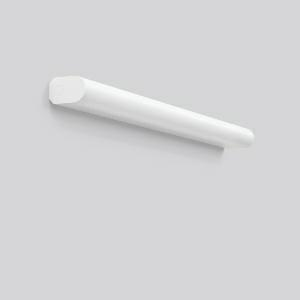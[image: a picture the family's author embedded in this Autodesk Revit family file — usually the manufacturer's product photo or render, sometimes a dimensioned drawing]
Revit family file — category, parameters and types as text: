
# Revit family: rt_44_451169_002_1e48
name_source: partatom
category: Lighting Fixtures
units: mm (PartAtom-declared; Revit-internal decimal feet)

## family parameters
Cut with Voids When Loaded = No
Host = Face
Light Source = No
Part Type = Normal
Room Calculation Point = No
Round Connector Dimension = Use Diameter
Shared = No

## types (1)
- RT 44 (1 x LED Modul 830, 1400 lm, 3000)
    Apparent Load = 15 VA
    CIE Flux Codes = 36 65 85 82 100
    Color Rendering = 80
    Color Temperature = 3000
    Default Elevation = 1800 mm
    Description = Series: RT 44
Linear luminaire, can be used as wall and mirror luminaire. Base: aluminium, powder-coated. End caps: plastic (polycarbonate), shock-resistant. Diffuser: plastic (polycarbonate), opal. Suitable for Ceiling mounting, Wall (surface). Can be installed horizontally and vertically. Very easy installation thanks to Plug+Play connection. Driver integrated. High type of protection: IP44 for use in wet areas. 
Colour: pure white (RAL 9010)
Length: 900 mm
Width: 55 mm
Height: 87 mm
Lamp: LED
Socket: without socket
Colour temperature: 3000K
Colour rendering index (CRI): 80
System power: 15 W
Rated luminous flux: 1400 lm
Luminous efficiency: 93 lm/W
Control gear: Regulated power supply
Protection class: I
Type of protection: IP 44
    Height = 87 mm
    Lamp = 1 x LED Modul 830
    Lamp Light Flux = 1400 lm
    Lamp count = 1
    Length = 900 mm
    Lifetime = 50000 h
    Luminous efficacy = 93 lm/W
    Manufacturer = RZB
    ModVariant = No
    Model = 451169.002
    Mounting Place = Ceiling, Wall
    Mounting Type = Surface mounted
    Number of Poles = 1
    OnlyDefault = Yes
    Power Factor = 1
    Product Name = RT 44
    Product group = Surface mounted ceiling and wall luminaires
    ProductGroupID = 305
    Protection Class = Protection class I
    Protection Degree = IP 44
    RLX_Detail_Level = 1
    RLX_Emergency_Light_Flux = 0 lm
    RLX_Emergency_Type = 0
    RLX_Emergency_Type_DB = No
    RlxData = <blob elided: 26889 chars, md5=8198606b>
    Socket = socket
    Standby Power = 0 W
    System Light Flux = 1400 lm
    System Power = 15 W
    Type Comments = Product without accessories
    Type Image = 451055.752.jpg
    URL = http://relux.com
    VarID = ---
    Voltage = 230 V
    Voltage Range = 220-240 V
    Weight = 0.00 kg
    Width = 55 mm

## geometry (parser evidence)
native form markers: Blend x4, Sweep x14
no freeform markers — native parametric forms only
